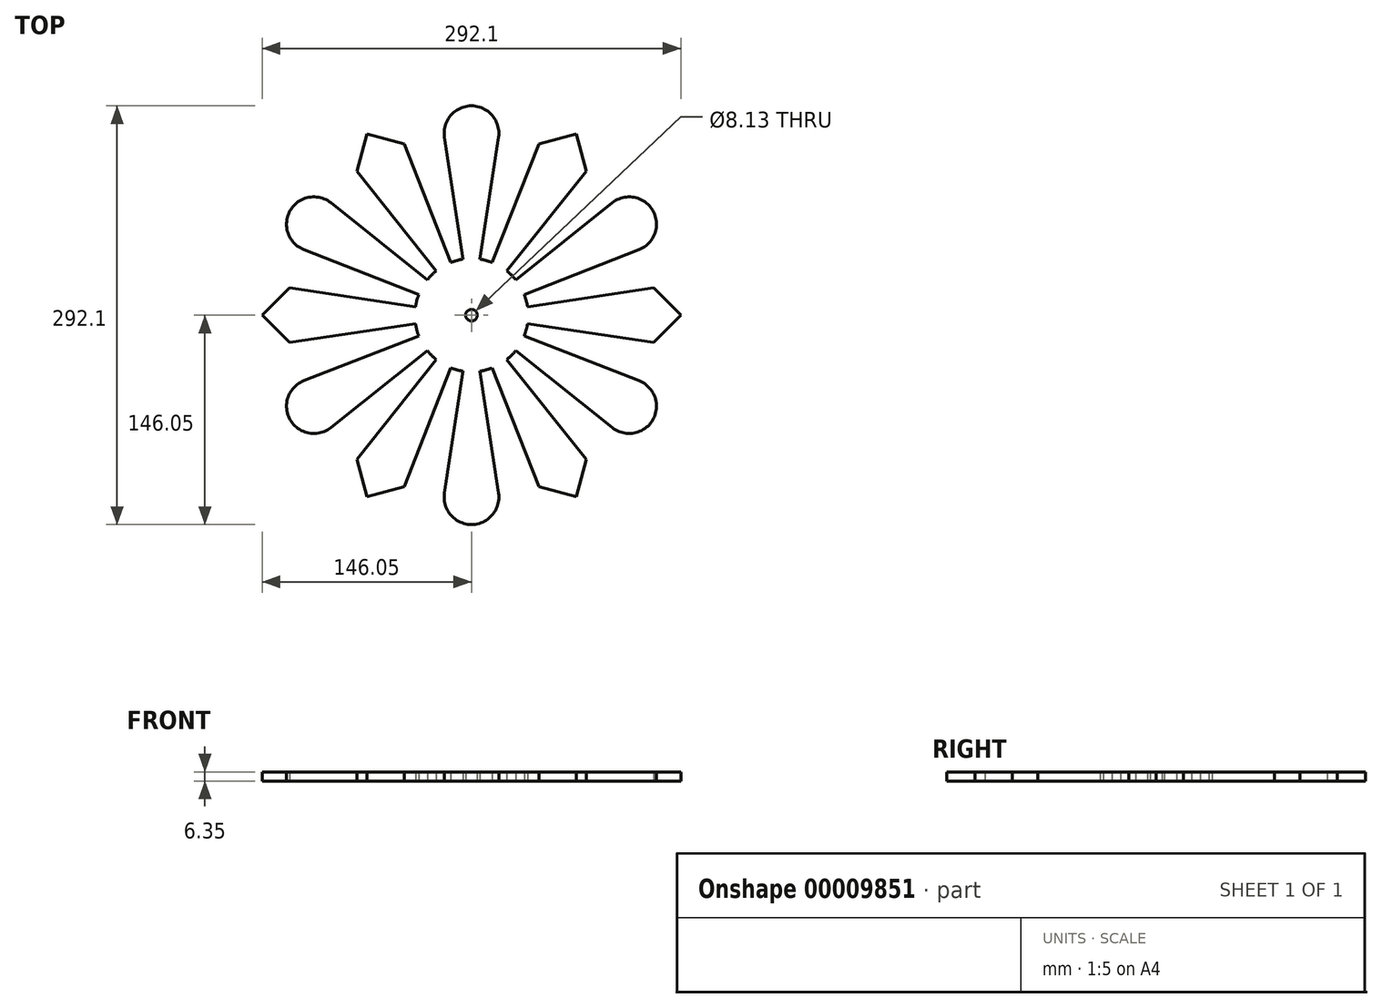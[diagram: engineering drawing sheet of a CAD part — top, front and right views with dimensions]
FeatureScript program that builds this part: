
annotation { "Feature Type Name" : "Feature", "Feature Type Description" : "" }
export const myFeature = defineFeature(function(context is Context, id is Id, definition is map)
    precondition{}
    {
        {
            var Q0;
            Q0=qCreatedBy(makeId("Top.planeOp"),FACE);
            var sketch = newSketch(context, id + "F0", { "sketchPlane" : qUnion([Q0])});
            skLineSegment(sketch, "E0.rect.bottom", {"start": v(203.2, 152.4) * mm, "end": v(-203.2, 152.4) * mm, "construction": true});
            skLineSegment(sketch, "E0.rect.top", {"start": v(203.2, -152.4) * mm, "end": v(-203.2, -152.4) * mm, "construction": true});
            skLineSegment(sketch, "E0.rect.left", {"start": v(203.2, 152.4) * mm, "end": v(203.2, -152.4) * mm, "construction": true});
            skLineSegment(sketch, "E0.rect.right", {"start": v(-203.2, 152.4) * mm, "end": v(-203.2, -152.4) * mm, "construction": true});
            skPoint(sketch, "E0.rect.middle", {"position": v(0, 0) * mm});
            skLineSegment(sketch, "E1.0", {"start": v(196.85, 146.05) * mm, "end": v(-196.85, 146.05) * mm, "construction": true});
            skLineSegment(sketch, "E1.1", {"start": v(196.85, 146.05) * mm, "end": v(196.85, -146.05) * mm, "construction": true});
            skLineSegment(sketch, "E1.2", {"start": v(196.85, -146.05) * mm, "end": v(-196.85, -146.05) * mm, "construction": true});
            skLineSegment(sketch, "E1.3", {"start": v(-196.85, 146.05) * mm, "end": v(-196.85, -146.05) * mm, "construction": true});
            skLineSegment(sketch, "E2.rect.bottom", {"start": v(-27.94, 27.94) * mm, "end": v(27.94, 27.94) * mm, "construction": true});
            skLineSegment(sketch, "E2.rect.top", {"start": v(-27.94, -27.94) * mm, "end": v(27.94, -27.94) * mm, "construction": true});
            skLineSegment(sketch, "E2.rect.left", {"start": v(-27.94, 27.94) * mm, "end": v(-27.94, -27.94) * mm, "construction": true});
            skLineSegment(sketch, "E2.rect.right", {"start": v(27.94, 27.94) * mm, "end": v(27.94, -27.94) * mm, "construction": true});
            skCircle(sketch, "E3", {"center": v(0, 0) * mm, "radius": 39.51 * mm});
            skCircle(sketch, "E4", {"center": v(0, 127) * mm, "radius": 19.05 * mm});
            skLineSegment(sketch, "E5", {"start": v(0, 0) * mm, "end": v(-18.83, 124.14) * mm});
            skLineSegment(sketch, "E6", {"start": v(0, 0) * mm, "end": v(18.83, 124.14) * mm});
            skLineSegment(sketch, "E7", {"start": v(0, 0) * mm, "end": v(0, 127) * mm, "construction": true});
            skLineSegment(sketch, "E8", {"start": v(0, 0) * mm, "end": v(63.5, 109.99) * mm, "construction": true});
            skLineSegment(sketch, "E9", {"start": v(47, 119.51) * mm, "end": v(80, 100.46) * mm, "construction": true});
            skLineSegment(sketch, "E10", {"start": v(0, 0) * mm, "end": v(47, 119.51) * mm});
            skLineSegment(sketch, "E11", {"start": v(80, 100.46) * mm, "end": v(0, 0) * mm});
            skLineSegment(sketch, "E12", {"start": v(47, 119.51) * mm, "end": v(73.03, 126.48) * mm});
            skLineSegment(sketch, "E13", {"start": v(73.03, 126.48) * mm, "end": v(80, 100.46) * mm});
            skLineSegment(sketch, "E14.1.0", {"start": v(0, 0) * mm, "end": v(-63.5, 109.99) * mm, "construction": true});
            skLineSegment(sketch, "E14.1.1", {"start": v(-80, 100.46) * mm, "end": v(-73.03, 126.48) * mm});
            skLineSegment(sketch, "E14.1.2", {"start": v(0, 0) * mm, "end": v(-109.99, 63.5) * mm, "construction": true});
            skLineSegment(sketch, "E14.1.4", {"start": v(-80, 100.46) * mm, "end": v(-47, 119.51) * mm, "construction": true});
            skLineSegment(sketch, "E14.1.5", {"start": v(-73.03, 126.48) * mm, "end": v(-47, 119.51) * mm});
            skLineSegment(sketch, "E14.1.6", {"start": v(-47, 119.51) * mm, "end": v(0, 0) * mm});
            skLineSegment(sketch, "E14.1.7", {"start": v(0, 0) * mm, "end": v(-98.1, 78.38) * mm});
            skLineSegment(sketch, "E14.1.8", {"start": v(0, 0) * mm, "end": v(-116.93, 45.76) * mm});
            skLineSegment(sketch, "E14.1.9", {"start": v(0, 0) * mm, "end": v(-80, 100.46) * mm});
            skCircle(sketch, "E14.1.10", {"center": v(-109.99, 63.5) * mm, "radius": 19.05 * mm});
            skLineSegment(sketch, "E14.2.0", {"start": v(0, 0) * mm, "end": v(-127, 0) * mm, "construction": true});
            skLineSegment(sketch, "E14.2.1", {"start": v(-127, -19.05) * mm, "end": v(-146.05, 0) * mm});
            skLineSegment(sketch, "E14.2.2", {"start": v(0, 0) * mm, "end": v(-109.99, -63.5) * mm, "construction": true});
            skLineSegment(sketch, "E14.2.4", {"start": v(-127, -19.05) * mm, "end": v(-127, 19.05) * mm, "construction": true});
            skLineSegment(sketch, "E14.2.5", {"start": v(-146.05, 0) * mm, "end": v(-127, 19.05) * mm});
            skLineSegment(sketch, "E14.2.6", {"start": v(-127, 19.05) * mm, "end": v(0, 0) * mm});
            skLineSegment(sketch, "E14.2.7", {"start": v(-116.93, -45.76) * mm, "end": v(0, 0) * mm});
            skLineSegment(sketch, "E14.2.8", {"start": v(0, 0) * mm, "end": v(-98.1, -78.38) * mm});
            skLineSegment(sketch, "E14.2.9", {"start": v(0, 0) * mm, "end": v(-127, -19.05) * mm});
            skCircle(sketch, "E14.2.10", {"center": v(-109.99, -63.5) * mm, "radius": 19.05 * mm});
            skLineSegment(sketch, "E15.1.3.0", {"start": v(0, 0) * mm, "end": v(-63.5, -109.99) * mm, "construction": true});
            skLineSegment(sketch, "E15.3.3.0", {"start": v(-47, -119.51) * mm, "end": v(-73.03, -126.48) * mm});
            skLineSegment(sketch, "E15.6.3.0", {"start": v(0, 0) * mm, "end": v(0, -127) * mm, "construction": true});
            skLineSegment(sketch, "E15.10.3.0", {"start": v(-47, -119.51) * mm, "end": v(-80, -100.46) * mm, "construction": true});
            skLineSegment(sketch, "E15.13.3.0", {"start": v(-73.03, -126.48) * mm, "end": v(-80, -100.46) * mm});
            skLineSegment(sketch, "E15.16.3.0", {"start": v(-80, -100.46) * mm, "end": v(0, 0) * mm});
            skLineSegment(sketch, "E15.19.3.0", {"start": v(0, 0) * mm, "end": v(-18.83, -124.14) * mm});
            skLineSegment(sketch, "E15.22.3.0", {"start": v(0, 0) * mm, "end": v(18.83, -124.14) * mm});
            skLineSegment(sketch, "E15.25.3.0", {"start": v(0, 0) * mm, "end": v(-47, -119.51) * mm});
            skCircle(sketch, "E15.28.3.0", {"center": v(0, -127) * mm, "radius": 19.05 * mm});
            skLineSegment(sketch, "E15.1.4.0", {"start": v(0, 0) * mm, "end": v(63.5, -109.99) * mm, "construction": true});
            skLineSegment(sketch, "E15.3.4.0", {"start": v(80, -100.46) * mm, "end": v(73.03, -126.48) * mm});
            skLineSegment(sketch, "E15.6.4.0", {"start": v(0, 0) * mm, "end": v(109.99, -63.5) * mm, "construction": true});
            skLineSegment(sketch, "E15.10.4.0", {"start": v(80, -100.46) * mm, "end": v(47, -119.51) * mm, "construction": true});
            skLineSegment(sketch, "E15.13.4.0", {"start": v(73.03, -126.48) * mm, "end": v(47, -119.51) * mm});
            skLineSegment(sketch, "E15.16.4.0", {"start": v(47, -119.51) * mm, "end": v(0, 0) * mm});
            skLineSegment(sketch, "E15.19.4.0", {"start": v(0, 0) * mm, "end": v(98.1, -78.38) * mm});
            skLineSegment(sketch, "E15.22.4.0", {"start": v(0, 0) * mm, "end": v(116.93, -45.76) * mm});
            skLineSegment(sketch, "E15.25.4.0", {"start": v(0, 0) * mm, "end": v(80, -100.46) * mm});
            skCircle(sketch, "E15.28.4.0", {"center": v(109.99, -63.5) * mm, "radius": 19.05 * mm});
            skLineSegment(sketch, "E15.1.5.0", {"start": v(0, 0) * mm, "end": v(127, 0) * mm, "construction": true});
            skLineSegment(sketch, "E15.3.5.0", {"start": v(127, 19.05) * mm, "end": v(146.05, 0) * mm});
            skLineSegment(sketch, "E15.6.5.0", {"start": v(0, 0) * mm, "end": v(109.99, 63.5) * mm, "construction": true});
            skLineSegment(sketch, "E15.10.5.0", {"start": v(127, 19.05) * mm, "end": v(127, -19.05) * mm, "construction": true});
            skLineSegment(sketch, "E15.13.5.0", {"start": v(146.05, 0) * mm, "end": v(127, -19.05) * mm});
            skLineSegment(sketch, "E15.16.5.0", {"start": v(127, -19.05) * mm, "end": v(0, 0) * mm});
            skLineSegment(sketch, "E15.19.5.0", {"start": v(116.93, 45.76) * mm, "end": v(0, 0) * mm});
            skLineSegment(sketch, "E15.22.5.0", {"start": v(0, 0) * mm, "end": v(98.1, 78.38) * mm});
            skLineSegment(sketch, "E15.25.5.0", {"start": v(0, 0) * mm, "end": v(127, 19.05) * mm});
            skCircle(sketch, "E15.28.5.0", {"center": v(109.99, 63.5) * mm, "radius": 19.05 * mm});
            skSolve(sketch);
        }
        {
            var Q0;
            {var subQ1=sQuery(id+"F0.wireOp",EDGE,"E3");var subQ5=sQuery(id+"F0.wireOp",EDGE,"E14.1.7");var subQ7=makeQuery(id+"F0.imprint","INTERSECT",VERTEX,{"derivedFrom":[subQ1,subQ5]});Q0=makeQuery(id+"F0.imprint","IMPRINT",FACE,{"disambiguationData":[TD([[makeQuery(id+"F0.imprint","IMPRINT",EDGE,{"disambiguationData":[TD([[subQ7,-1.0]])],"derivedFrom":subQ1}),-1.0]])]});}
            var Q1;
            {var subQ3=sQuery(id+"F0.wireOp",EDGE,"E15.3.5.0");Q1=makeQuery(id+"F0.imprint","IMPRINT",FACE,{"disambiguationData":[TD([[makeQuery(id+"F0.imprint","IMPRINT",EDGE,{"derivedFrom":subQ3}),-1.0]])]});}
            var Q2;
            {var subQ3=sQuery(id+"F0.wireOp",EDGE,"E15.3.3.0");Q2=makeQuery(id+"F0.imprint","IMPRINT",FACE,{"disambiguationData":[TD([[makeQuery(id+"F0.imprint","IMPRINT",EDGE,{"derivedFrom":subQ3}),-1.0]])]});}
            var Q3;
            {var subQ3=sQuery(id+"F0.wireOp",EDGE,"E15.3.4.0");Q3=makeQuery(id+"F0.imprint","IMPRINT",FACE,{"disambiguationData":[TD([[makeQuery(id+"F0.imprint","IMPRINT",EDGE,{"derivedFrom":subQ3}),-1.0]])]});}
            var Q4;
            {var subQ0=sQuery(id+"F0.wireOp",EDGE,"E14.2.10");var subQ2=makeQuery(id+"F0.imprint","INTERSECT",VERTEX,{"derivedFrom":[sQuery(id+"F0.wireOp",EDGE,"E14.2.7"),subQ0]});Q4=makeQuery(id+"F0.imprint","IMPRINT",FACE,{"disambiguationData":[TD([[makeQuery(id+"F0.imprint","IMPRINT",EDGE,{"disambiguationData":[TD([[subQ2,1.0]])],"derivedFrom":subQ0}),1.0]])]});}
            var Q5;
            {var subQ6=sQuery(id+"F0.wireOp",EDGE,"E14.2.1");Q5=makeQuery(id+"F0.imprint","IMPRINT",FACE,{"disambiguationData":[TD([[makeQuery(id+"F0.imprint","IMPRINT",EDGE,{"derivedFrom":subQ6}),-1.0]])]});}
            var Q6;
            {var subQ3=sQuery(id+"F0.wireOp",EDGE,"E14.1.1");Q6=makeQuery(id+"F0.imprint","IMPRINT",FACE,{"disambiguationData":[TD([[makeQuery(id+"F0.imprint","IMPRINT",EDGE,{"derivedFrom":subQ3}),-1.0]])]});}
            var Q7;
            {var subQ0=sQuery(id+"F0.wireOp",EDGE,"E15.28.3.0");var subQ2=makeQuery(id+"F0.imprint","INTERSECT",VERTEX,{"derivedFrom":[sQuery(id+"F0.wireOp",EDGE,"E15.19.3.0"),subQ0]});Q7=makeQuery(id+"F0.imprint","IMPRINT",FACE,{"disambiguationData":[TD([[makeQuery(id+"F0.imprint","IMPRINT",EDGE,{"disambiguationData":[TD([[subQ2,1.0]])],"derivedFrom":subQ0}),1.0]])]});}
            var Q8;
            {var subQ1=sQuery(id+"F0.wireOp",EDGE,"E3");var subQ3=sQuery(id+"F0.wireOp",EDGE,"E15.22.4.0");var subQ5=makeQuery(id+"F0.imprint","INTERSECT",VERTEX,{"derivedFrom":[subQ1,subQ3]});Q8=makeQuery(id+"F0.imprint","IMPRINT",FACE,{"disambiguationData":[TD([[makeQuery(id+"F0.imprint","IMPRINT",EDGE,{"disambiguationData":[TD([[subQ5,-1.0]])],"derivedFrom":subQ1}),1.0]])]});}
            var Q9;
            {var subQ1=sQuery(id+"F0.wireOp",EDGE,"E3");var subQ3=sQuery(id+"F0.wireOp",EDGE,"E14.1.8");var subQ5=makeQuery(id+"F0.imprint","INTERSECT",VERTEX,{"derivedFrom":[subQ1,subQ3]});Q9=makeQuery(id+"F0.imprint","IMPRINT",FACE,{"disambiguationData":[TD([[makeQuery(id+"F0.imprint","IMPRINT",EDGE,{"disambiguationData":[TD([[subQ5,-1.0]])],"derivedFrom":subQ1}),1.0]])]});}
            var Q10;
            {var subQ3=sQuery(id+"F0.wireOp",EDGE,"E15.19.4.0");var subQ5=sQuery(id+"F0.wireOp",EDGE,"E3");var subQ7=makeQuery(id+"F0.imprint","INTERSECT",VERTEX,{"derivedFrom":[subQ5,subQ3]});Q10=makeQuery(id+"F0.imprint","IMPRINT",FACE,{"disambiguationData":[TD([[makeQuery(id+"F0.imprint","IMPRINT",EDGE,{"disambiguationData":[TD([[subQ7,-1.0]])],"derivedFrom":subQ5}),-1.0]])]});}
            var Q11;
            {var subQ3=sQuery(id+"F0.wireOp",EDGE,"E15.19.3.0");var subQ5=sQuery(id+"F0.wireOp",EDGE,"E3");var subQ7=makeQuery(id+"F0.imprint","INTERSECT",VERTEX,{"derivedFrom":[subQ5,subQ3]});Q11=makeQuery(id+"F0.imprint","IMPRINT",FACE,{"disambiguationData":[TD([[makeQuery(id+"F0.imprint","IMPRINT",EDGE,{"disambiguationData":[TD([[subQ7,-1.0]])],"derivedFrom":subQ5}),-1.0]])]});}
            var Q12;
            {var subQ1=sQuery(id+"F0.wireOp",EDGE,"E12");Q12=makeQuery(id+"F0.imprint","IMPRINT",FACE,{"disambiguationData":[TD([[makeQuery(id+"F0.imprint","IMPRINT",EDGE,{"derivedFrom":subQ1}),-1.0]])]});}
            var Q13;
            {var subQ1=sQuery(id+"F0.wireOp",EDGE,"E3");var subQ3=sQuery(id+"F0.wireOp",EDGE,"E5");var subQ5=makeQuery(id+"F0.imprint","INTERSECT",VERTEX,{"derivedFrom":[subQ1,subQ3]});Q13=makeQuery(id+"F0.imprint","IMPRINT",FACE,{"disambiguationData":[TD([[makeQuery(id+"F0.imprint","IMPRINT",EDGE,{"disambiguationData":[TD([[subQ5,-1.0]])],"derivedFrom":subQ1}),1.0]])]});}
            var Q14;
            {var subQ0=sQuery(id+"F0.wireOp",EDGE,"E14.1.10");var subQ2=makeQuery(id+"F0.imprint","INTERSECT",VERTEX,{"derivedFrom":[sQuery(id+"F0.wireOp",EDGE,"E14.1.7"),subQ0]});Q14=makeQuery(id+"F0.imprint","IMPRINT",FACE,{"disambiguationData":[TD([[makeQuery(id+"F0.imprint","IMPRINT",EDGE,{"disambiguationData":[TD([[subQ2,1.0]])],"derivedFrom":subQ0}),1.0]])]});}
            var Q15;
            {var subQ0=sQuery(id+"F0.wireOp",EDGE,"E4");var subQ2=makeQuery(id+"F0.imprint","INTERSECT",VERTEX,{"derivedFrom":[subQ0,sQuery(id+"F0.wireOp",EDGE,"E5")]});Q15=makeQuery(id+"F0.imprint","IMPRINT",FACE,{"disambiguationData":[TD([[makeQuery(id+"F0.imprint","IMPRINT",EDGE,{"disambiguationData":[TD([[subQ2,-1.0]])],"derivedFrom":subQ0}),1.0]])]});}
            var Q16;
            {var subQ3=sQuery(id+"F0.wireOp",EDGE,"E15.19.5.0");var subQ5=sQuery(id+"F0.wireOp",EDGE,"E3");var subQ7=makeQuery(id+"F0.imprint","INTERSECT",VERTEX,{"derivedFrom":[subQ5,subQ3]});Q16=makeQuery(id+"F0.imprint","IMPRINT",FACE,{"disambiguationData":[TD([[makeQuery(id+"F0.imprint","IMPRINT",EDGE,{"disambiguationData":[TD([[subQ7,-1.0]])],"derivedFrom":subQ5}),-1.0]])]});}
            var Q17;
            {var subQ1=sQuery(id+"F0.wireOp",EDGE,"E3");var subQ3=sQuery(id+"F0.wireOp",EDGE,"E15.22.3.0");var subQ5=makeQuery(id+"F0.imprint","INTERSECT",VERTEX,{"derivedFrom":[subQ1,subQ3]});Q17=makeQuery(id+"F0.imprint","IMPRINT",FACE,{"disambiguationData":[TD([[makeQuery(id+"F0.imprint","IMPRINT",EDGE,{"disambiguationData":[TD([[subQ5,-1.0]])],"derivedFrom":subQ1}),1.0]])]});}
            var Q18;
            {var subQ0=sQuery(id+"F0.wireOp",EDGE,"E15.28.4.0");var subQ2=makeQuery(id+"F0.imprint","INTERSECT",VERTEX,{"derivedFrom":[sQuery(id+"F0.wireOp",EDGE,"E15.19.4.0"),subQ0]});Q18=makeQuery(id+"F0.imprint","IMPRINT",FACE,{"disambiguationData":[TD([[makeQuery(id+"F0.imprint","IMPRINT",EDGE,{"disambiguationData":[TD([[subQ2,1.0]])],"derivedFrom":subQ0}),1.0]])]});}
            var Q19;
            {var subQ3=sQuery(id+"F0.wireOp",EDGE,"E14.2.7");var subQ5=sQuery(id+"F0.wireOp",EDGE,"E3");var subQ7=makeQuery(id+"F0.imprint","INTERSECT",VERTEX,{"derivedFrom":[subQ5,subQ3]});Q19=makeQuery(id+"F0.imprint","IMPRINT",FACE,{"disambiguationData":[TD([[makeQuery(id+"F0.imprint","IMPRINT",EDGE,{"disambiguationData":[TD([[subQ7,-1.0]])],"derivedFrom":subQ5}),-1.0]])]});}
            var Q20;
            {var subQ0=sQuery(id+"F0.wireOp",EDGE,"E6");var subQ1=sQuery(id+"F0.wireOp",EDGE,"E3");var subQ2=makeQuery(id+"F0.imprint","INTERSECT",VERTEX,{"derivedFrom":[subQ1,subQ0]});Q20=makeQuery(id+"F0.imprint","IMPRINT",FACE,{"disambiguationData":[TD([[makeQuery(id+"F0.imprint","IMPRINT",EDGE,{"disambiguationData":[TD([[subQ2,-1.0]])],"derivedFrom":subQ1}),-1.0]])]});}
            var Q21;
            {var subQ0=sQuery(id+"F0.wireOp",EDGE,"E15.28.5.0");var subQ2=makeQuery(id+"F0.imprint","INTERSECT",VERTEX,{"derivedFrom":[sQuery(id+"F0.wireOp",EDGE,"E15.19.5.0"),subQ0]});Q21=makeQuery(id+"F0.imprint","IMPRINT",FACE,{"disambiguationData":[TD([[makeQuery(id+"F0.imprint","IMPRINT",EDGE,{"disambiguationData":[TD([[subQ2,1.0]])],"derivedFrom":subQ0}),1.0]])]});}
            var Q22;
            {var subQ1=sQuery(id+"F0.wireOp",EDGE,"E3");var subQ3=sQuery(id+"F0.wireOp",EDGE,"E14.2.6");var subQ5=makeQuery(id+"F0.imprint","INTERSECT",VERTEX,{"derivedFrom":[subQ1,subQ3]});Q22=makeQuery(id+"F0.imprint","IMPRINT",FACE,{"disambiguationData":[TD([[makeQuery(id+"F0.imprint","IMPRINT",EDGE,{"disambiguationData":[TD([[subQ5,-1.0]])],"derivedFrom":subQ1}),1.0]])]});}
            var Q23;
            {var subQ1=sQuery(id+"F0.wireOp",EDGE,"E3");var subQ3=sQuery(id+"F0.wireOp",EDGE,"E15.19.5.0");var subQ5=makeQuery(id+"F0.imprint","INTERSECT",VERTEX,{"derivedFrom":[subQ1,subQ3]});Q23=makeQuery(id+"F0.imprint","IMPRINT",FACE,{"disambiguationData":[TD([[makeQuery(id+"F0.imprint","IMPRINT",EDGE,{"disambiguationData":[TD([[subQ5,-1.0]])],"derivedFrom":subQ1}),1.0]])]});}
            var Q24;
            {var subQ0=sQuery(id+"F0.wireOp",EDGE,"E14.2.7");var subQ1=sQuery(id+"F0.wireOp",EDGE,"E3");var subQ2=makeQuery(id+"F0.imprint","INTERSECT",VERTEX,{"derivedFrom":[subQ1,subQ0]});Q24=makeQuery(id+"F0.imprint","IMPRINT",FACE,{"disambiguationData":[TD([[makeQuery(id+"F0.imprint","IMPRINT",EDGE,{"disambiguationData":[TD([[subQ2,-1.0]])],"derivedFrom":subQ1}),1.0]])]});}
            var Q25;
            {var subQ0=sQuery(id+"F0.wireOp",EDGE,"E11");var subQ1=sQuery(id+"F0.wireOp",EDGE,"E3");var subQ2=makeQuery(id+"F0.imprint","INTERSECT",VERTEX,{"derivedFrom":[subQ1,subQ0]});Q25=makeQuery(id+"F0.imprint","IMPRINT",FACE,{"disambiguationData":[TD([[makeQuery(id+"F0.imprint","IMPRINT",EDGE,{"disambiguationData":[TD([[subQ2,-1.0]])],"derivedFrom":subQ1}),1.0]])]});}
            var Q26;
            {var subQ0=sQuery(id+"F0.wireOp",EDGE,"E15.25.5.0");var subQ1=sQuery(id+"F0.wireOp",EDGE,"E3");var subQ2=makeQuery(id+"F0.imprint","INTERSECT",VERTEX,{"derivedFrom":[subQ1,subQ0]});Q26=makeQuery(id+"F0.imprint","IMPRINT",FACE,{"disambiguationData":[TD([[makeQuery(id+"F0.imprint","IMPRINT",EDGE,{"disambiguationData":[TD([[subQ2,1.0]])],"derivedFrom":subQ1}),1.0]])]});}
            var Q27;
            {var subQ1=sQuery(id+"F0.wireOp",EDGE,"E3");var subQ3=sQuery(id+"F0.wireOp",EDGE,"E15.19.4.0");var subQ5=makeQuery(id+"F0.imprint","INTERSECT",VERTEX,{"derivedFrom":[subQ1,subQ3]});Q27=makeQuery(id+"F0.imprint","IMPRINT",FACE,{"disambiguationData":[TD([[makeQuery(id+"F0.imprint","IMPRINT",EDGE,{"disambiguationData":[TD([[subQ5,-1.0]])],"derivedFrom":subQ1}),1.0]])]});}
            var Q28;
            {var subQ0=sQuery(id+"F0.wireOp",EDGE,"E15.25.3.0");var subQ1=sQuery(id+"F0.wireOp",EDGE,"E3");var subQ2=makeQuery(id+"F0.imprint","INTERSECT",VERTEX,{"derivedFrom":[subQ1,subQ0]});Q28=makeQuery(id+"F0.imprint","IMPRINT",FACE,{"disambiguationData":[TD([[makeQuery(id+"F0.imprint","IMPRINT",EDGE,{"disambiguationData":[TD([[subQ2,-1.0]])],"derivedFrom":subQ1}),1.0]])]});}
            var Q29;
            {var subQ0=sQuery(id+"F0.wireOp",EDGE,"E15.22.5.0");var subQ1=sQuery(id+"F0.wireOp",EDGE,"E3");var subQ2=makeQuery(id+"F0.imprint","INTERSECT",VERTEX,{"derivedFrom":[subQ1,subQ0]});Q29=makeQuery(id+"F0.imprint","IMPRINT",FACE,{"disambiguationData":[TD([[makeQuery(id+"F0.imprint","IMPRINT",EDGE,{"disambiguationData":[TD([[subQ2,-1.0]])],"derivedFrom":subQ1}),1.0]])]});}
            var Q30;
            {var subQ1=sQuery(id+"F0.wireOp",EDGE,"E3");var subQ3=sQuery(id+"F0.wireOp",EDGE,"E14.1.6");var subQ5=makeQuery(id+"F0.imprint","INTERSECT",VERTEX,{"derivedFrom":[subQ1,subQ3]});Q30=makeQuery(id+"F0.imprint","IMPRINT",FACE,{"disambiguationData":[TD([[makeQuery(id+"F0.imprint","IMPRINT",EDGE,{"disambiguationData":[TD([[subQ5,-1.0]])],"derivedFrom":subQ1}),1.0]])]});}
            var Q31;
            {var subQ1=sQuery(id+"F0.wireOp",EDGE,"E3");var subQ3=sQuery(id+"F0.wireOp",EDGE,"E14.1.7");var subQ5=makeQuery(id+"F0.imprint","INTERSECT",VERTEX,{"derivedFrom":[subQ1,subQ3]});Q31=makeQuery(id+"F0.imprint","IMPRINT",FACE,{"disambiguationData":[TD([[makeQuery(id+"F0.imprint","IMPRINT",EDGE,{"disambiguationData":[TD([[subQ5,-1.0]])],"derivedFrom":subQ1}),1.0]])]});}
            var Q32;
            {var subQ0=sQuery(id+"F0.wireOp",EDGE,"E15.25.4.0");var subQ1=sQuery(id+"F0.wireOp",EDGE,"E3");var subQ2=makeQuery(id+"F0.imprint","INTERSECT",VERTEX,{"derivedFrom":[subQ1,subQ0]});Q32=makeQuery(id+"F0.imprint","IMPRINT",FACE,{"disambiguationData":[TD([[makeQuery(id+"F0.imprint","IMPRINT",EDGE,{"disambiguationData":[TD([[subQ2,-1.0]])],"derivedFrom":subQ1}),1.0]])]});}
            var Q33;
            {var subQ1=sQuery(id+"F0.wireOp",EDGE,"E3");var subQ3=sQuery(id+"F0.wireOp",EDGE,"E15.16.3.0");var subQ5=makeQuery(id+"F0.imprint","INTERSECT",VERTEX,{"derivedFrom":[subQ1,subQ3]});Q33=makeQuery(id+"F0.imprint","IMPRINT",FACE,{"disambiguationData":[TD([[makeQuery(id+"F0.imprint","IMPRINT",EDGE,{"disambiguationData":[TD([[subQ5,-1.0]])],"derivedFrom":subQ1}),1.0]])]});}
            var Q34;
            {var subQ0=sQuery(id+"F0.wireOp",EDGE,"E14.2.9");var subQ1=sQuery(id+"F0.wireOp",EDGE,"E3");var subQ2=makeQuery(id+"F0.imprint","INTERSECT",VERTEX,{"derivedFrom":[subQ1,subQ0]});Q34=makeQuery(id+"F0.imprint","IMPRINT",FACE,{"disambiguationData":[TD([[makeQuery(id+"F0.imprint","IMPRINT",EDGE,{"disambiguationData":[TD([[subQ2,-1.0]])],"derivedFrom":subQ1}),1.0]])]});}
            var Q35;
            {var subQ1=sQuery(id+"F0.wireOp",EDGE,"E3");var subQ3=sQuery(id+"F0.wireOp",EDGE,"E15.19.3.0");var subQ5=makeQuery(id+"F0.imprint","INTERSECT",VERTEX,{"derivedFrom":[subQ1,subQ3]});Q35=makeQuery(id+"F0.imprint","IMPRINT",FACE,{"disambiguationData":[TD([[makeQuery(id+"F0.imprint","IMPRINT",EDGE,{"disambiguationData":[TD([[subQ5,-1.0]])],"derivedFrom":subQ1}),1.0]])]});}
            var Q36;
            {var subQ1=sQuery(id+"F0.wireOp",EDGE,"E3");var subQ3=sQuery(id+"F0.wireOp",EDGE,"E14.2.8");var subQ5=makeQuery(id+"F0.imprint","INTERSECT",VERTEX,{"derivedFrom":[subQ1,subQ3]});Q36=makeQuery(id+"F0.imprint","IMPRINT",FACE,{"disambiguationData":[TD([[makeQuery(id+"F0.imprint","IMPRINT",EDGE,{"disambiguationData":[TD([[subQ5,-1.0]])],"derivedFrom":subQ1}),1.0]])]});}
            var Q37;
            {var subQ1=sQuery(id+"F0.wireOp",EDGE,"E3");var subQ3=sQuery(id+"F0.wireOp",EDGE,"E15.16.4.0");var subQ5=makeQuery(id+"F0.imprint","INTERSECT",VERTEX,{"derivedFrom":[subQ1,subQ3]});Q37=makeQuery(id+"F0.imprint","IMPRINT",FACE,{"disambiguationData":[TD([[makeQuery(id+"F0.imprint","IMPRINT",EDGE,{"disambiguationData":[TD([[subQ5,-1.0]])],"derivedFrom":subQ1}),1.0]])]});}
            var Q38;
            {var subQ0=sQuery(id+"F0.wireOp",EDGE,"E6");var subQ1=sQuery(id+"F0.wireOp",EDGE,"E3");var subQ2=makeQuery(id+"F0.imprint","INTERSECT",VERTEX,{"derivedFrom":[subQ1,subQ0]});Q38=makeQuery(id+"F0.imprint","IMPRINT",FACE,{"disambiguationData":[TD([[makeQuery(id+"F0.imprint","IMPRINT",EDGE,{"disambiguationData":[TD([[subQ2,-1.0]])],"derivedFrom":subQ1}),1.0]])]});}
            var Q39;
            {var subQ0=sQuery(id+"F0.wireOp",EDGE,"E10");var subQ1=sQuery(id+"F0.wireOp",EDGE,"E3");var subQ2=makeQuery(id+"F0.imprint","INTERSECT",VERTEX,{"derivedFrom":[subQ1,subQ0]});Q39=makeQuery(id+"F0.imprint","IMPRINT",FACE,{"disambiguationData":[TD([[makeQuery(id+"F0.imprint","IMPRINT",EDGE,{"disambiguationData":[TD([[subQ2,-1.0]])],"derivedFrom":subQ1}),1.0]])]});}
            var Q40;
            {var subQ0=sQuery(id+"F0.wireOp",EDGE,"E14.1.9");var subQ1=sQuery(id+"F0.wireOp",EDGE,"E3");var subQ2=makeQuery(id+"F0.imprint","INTERSECT",VERTEX,{"derivedFrom":[subQ1,subQ0]});Q40=makeQuery(id+"F0.imprint","IMPRINT",FACE,{"disambiguationData":[TD([[makeQuery(id+"F0.imprint","IMPRINT",EDGE,{"disambiguationData":[TD([[subQ2,-1.0]])],"derivedFrom":subQ1}),1.0]])]});}
            var Q41;
            {var subQ1=sQuery(id+"F0.wireOp",EDGE,"E3");var subQ3=sQuery(id+"F0.wireOp",EDGE,"E15.19.5.0");var subQ5=makeQuery(id+"F0.imprint","INTERSECT",VERTEX,{"derivedFrom":[subQ1,subQ3]});Q41=makeQuery(id+"F0.imprint","IMPRINT",FACE,{"disambiguationData":[TD([[makeQuery(id+"F0.imprint","IMPRINT",EDGE,{"disambiguationData":[TD([[subQ5,1.0]])],"derivedFrom":subQ1}),1.0]])]});}
            extrude(context, id + "F1", {"entities" : qUnion([Q0, Q1, Q2, Q3, Q4, Q5, Q6, Q7, Q8, Q9, Q10, Q11, Q12, Q13, Q14, Q15, Q16, Q17, Q18, Q19, Q20, Q21, Q22, Q23, Q24, Q25, Q26, Q27, Q28, Q29, Q30, Q31, Q32, Q33, Q34, Q35, Q36, Q37, Q38, Q39, Q40, Q41]), "depth" : 6.35 * mm});
        }
        {
            var Q0;
            Q0=qCreatedBy(makeId("Top.planeOp"),FACE);
            var sketch = newSketch(context, id + "F2", { "sketchPlane" : qUnion([Q0])});
            skCircle(sketch, "E16", {"center": v(0, 0) * mm, "radius": 4.06 * mm});
            skSolve(sketch);
        }
        {
            var Q0;
            Q0=makeQuery(id+"F2.imprint","IMPRINT",FACE,{"disambiguationData":[TD([[makeQuery(id+"F2.imprint","IMPRINT",EDGE,{"derivedFrom":sQuery(id+"F2.wireOp",EDGE,"E16")}),1.0]])]});
            extrude(context, id + "F3", {"entities" : qUnion([Q0]), "operationType" : NewBodyOperationType.REMOVE, "endBound" : BoundingType.THROUGH_ALL, "depth" : 25.4 * mm});
        }
    });
